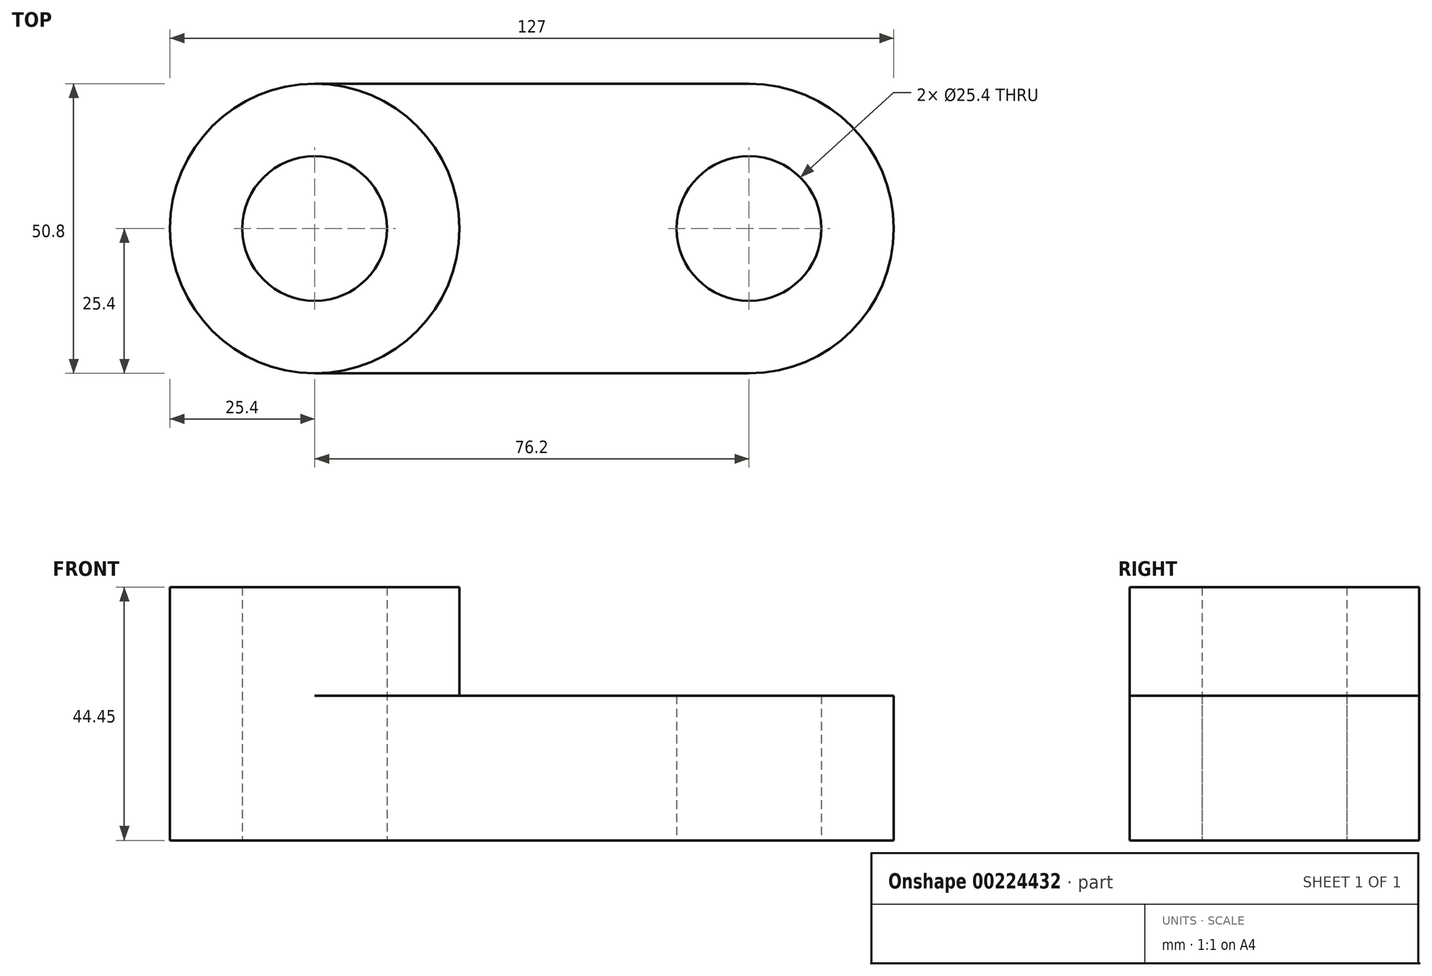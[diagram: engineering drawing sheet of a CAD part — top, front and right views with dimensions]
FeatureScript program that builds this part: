
annotation { "Feature Type Name" : "Feature", "Feature Type Description" : "" }
export const myFeature = defineFeature(function(context is Context, id is Id, definition is map)
    precondition{}
    {
        {
            var Q0;
            Q0=qCreatedBy(makeId("Top.planeOp"),FACE);
            var sketch = newSketch(context, id + "F0", { "sketchPlane" : qUnion([Q0])});
            skLineSegment(sketch, "E0.bottom", {"start": v(-38.1, -25.4) * mm, "end": v(38.1, -25.4) * mm});
            skLineSegment(sketch, "E0.top", {"start": v(-38.1, 25.4) * mm, "end": v(38.1, 25.4) * mm});
            skPoint(sketch, "E0.middle", {"position": v(0, 0) * mm});
            skCircle(sketch, "E1", {"center": v(-38.1, 0) * mm, "radius": 25.4 * mm});
            skArc(sketch, "E2", {"start": v(38.1, -25.4) * mm, "mid": v(63.5, 0) * mm, "end": v(38.1, 25.4) * mm});
            skCircle(sketch, "E3", {"center": v(-38.1, 0) * mm, "radius": 12.7 * mm});
            skCircle(sketch, "E4", {"center": v(38.1, 0) * mm, "radius": 12.7 * mm});
            skLineSegment(sketch, "E5", {"start": v(-38.1, 25.4) * mm, "end": v(-38.1, -25.4) * mm});
            skLineSegment(sketch, "E6", {"start": v(38.1, 25.4) * mm, "end": v(38.1, -25.4) * mm});
            skSolve(sketch);
        }
        {
            var Q0;
            {var subQ0=sQuery(id+"F0.wireOp",EDGE,"E5");var subQ4=sQuery(id+"F0.wireOp",EDGE,"E3");var subQ5=makeQuery(id+"F0.imprint","INTERSECT",VERTEX,{"disambiguationData":[OD(0.0)],"derivedFrom":[subQ4,subQ0]});Q0=makeQuery(id+"F0.imprint","IMPRINT",FACE,{"disambiguationData":[TD([[makeQuery(id+"F0.imprint","IMPRINT",EDGE,{"disambiguationData":[TD([[subQ5,-1.0]])],"derivedFrom":subQ4}),-1.0]])]});}
            var Q1;
            {var subQ0=sQuery(id+"F0.wireOp",EDGE,"E5");var subQ4=sQuery(id+"F0.wireOp",EDGE,"E3");var subQ5=makeQuery(id+"F0.imprint","INTERSECT",VERTEX,{"disambiguationData":[OD(0.0)],"derivedFrom":[subQ4,subQ0]});Q1=makeQuery(id+"F0.imprint","IMPRINT",FACE,{"disambiguationData":[TD([[makeQuery(id+"F0.imprint","IMPRINT",EDGE,{"disambiguationData":[TD([[subQ5,1.0]])],"derivedFrom":subQ4}),-1.0]])]});}
            extrude(context, id + "F1", {"entities" : qUnion([Q0, Q1]), "depth" : 44.45 * mm});
        }
        {
            var Q0;
            Q0 = qSketchRegion(id + "F0", true);
            extrude(context, id + "F2", {"entities" : qUnion([Q0]), "operationType" : NewBodyOperationType.ADD, "depth" : 25.4 * mm});
        }
    });
